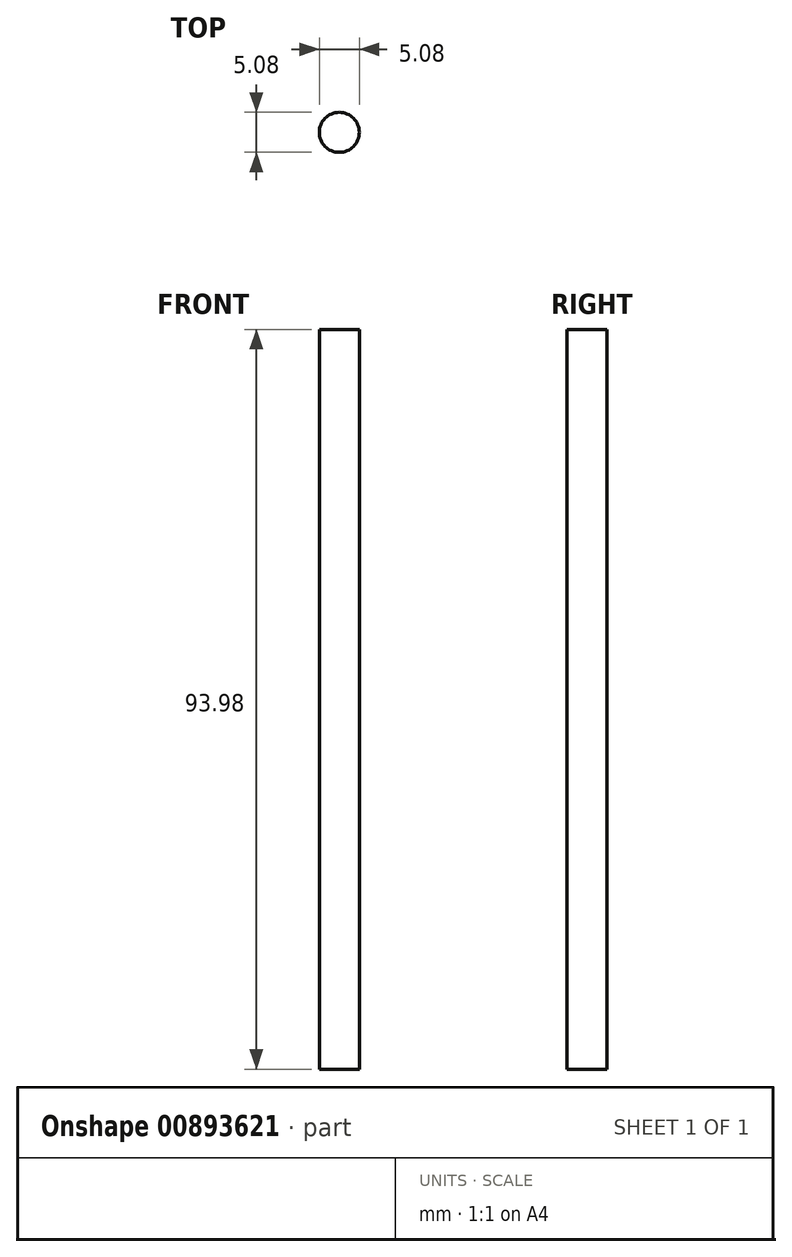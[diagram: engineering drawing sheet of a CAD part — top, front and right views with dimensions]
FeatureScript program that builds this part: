
annotation { "Feature Type Name" : "Feature", "Feature Type Description" : "" }
export const myFeature = defineFeature(function(context is Context, id is Id, definition is map)
    precondition{}
    {
        {
            var Q0;
            Q0=qCreatedBy(makeId("Top.planeOp"),FACE);
            var sketch = newSketch(context, id + "F0", { "sketchPlane" : qUnion([Q0])});
            skCircle(sketch, "E0", {"center": v(0, 0) * mm, "radius": 2.54 * mm});
            skSolve(sketch);
        }
        {
            var Q0;
            Q0 = qSketchRegion(id + "F0", true);
            extrude(context, id + "F1", {"entities" : qUnion([Q0]), "depth" : 93.98 * mm, "offsetDistance" : 25.4 * mm});
        }
    });
